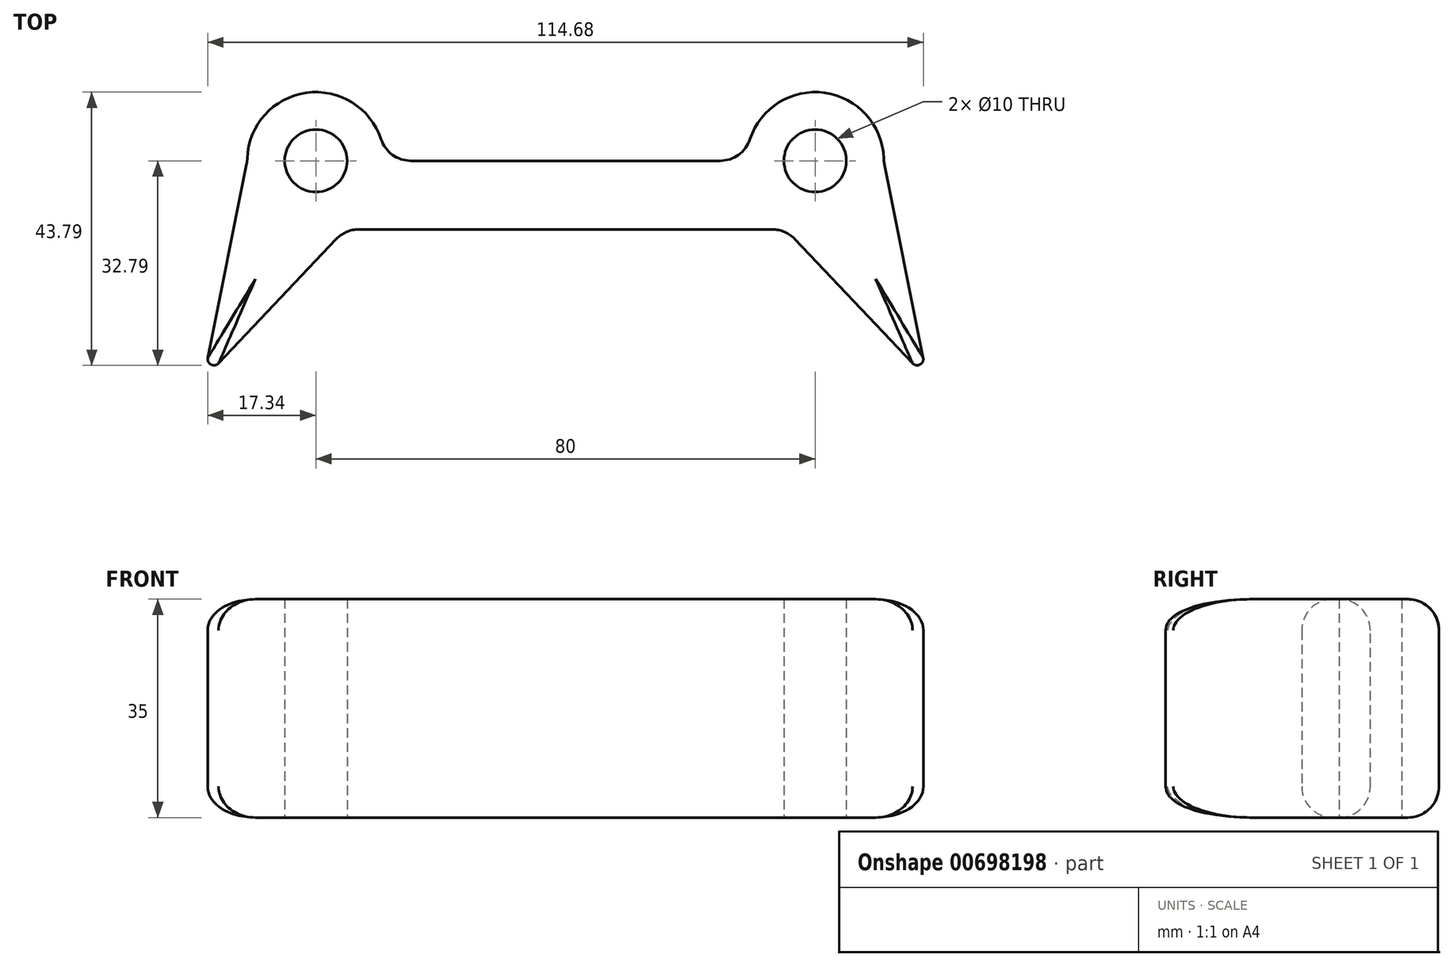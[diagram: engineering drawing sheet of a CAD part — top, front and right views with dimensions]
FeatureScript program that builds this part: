
annotation { "Feature Type Name" : "Feature", "Feature Type Description" : "" }
export const myFeature = defineFeature(function(context is Context, id is Id, definition is map)
    precondition{}
    {
        {
            var Q0;
            Q0=qCreatedBy(makeId("Top.planeOp"),FACE);
            var sketch = newSketch(context, id + "F0", { "sketchPlane" : qUnion([Q0])});
            skCircle(sketch, "E0", {"center": v(-40, 0) * mm, "radius": 5 * mm});
            skLineSegment(sketch, "E1", {"start": v(-35.27, -11) * mm, "end": v(0, -11) * mm});
            skLineSegment(sketch, "E2", {"start": v(-29, 0) * mm, "end": v(0, 0) * mm});
            skLineSegment(sketch, "E3", {"start": v(-51, 0) * mm, "end": v(-58, -35) * mm});
            skLineSegment(sketch, "E4", {"start": v(-58, -35) * mm, "end": v(-35.27, -11) * mm});
            skArc(sketch, "E5.trimOffspring", {"start": v(-29, 0) * mm, "mid": v(-40, 11) * mm, "end": v(-51, 0) * mm});
            skCircle(sketch, "E6.MirrorC", {"center": v(40, 0) * mm, "radius": 5 * mm});
            skLineSegment(sketch, "E7.MirrorCS", {"start": v(35.27, -11) * mm, "end": v(0, -11) * mm});
            skLineSegment(sketch, "E8.MirrorCS", {"start": v(29, 0) * mm, "end": v(0, 0) * mm});
            skLineSegment(sketch, "E9.MirrorCS", {"start": v(51, 0) * mm, "end": v(58, -35) * mm});
            skLineSegment(sketch, "E10.MirrorCS", {"start": v(58, -35) * mm, "end": v(35.27, -11) * mm});
            skArc(sketch, "E11.MirrorCS", {"start": v(29, 0) * mm, "mid": v(40, 11) * mm, "end": v(51, 0) * mm});
            skSolve(sketch);
        }
        {
            var Q0;
            Q0 = qSketchRegion(id + "F0", true);
            extrude(context, id + "F1", {"entities" : qUnion([Q0]), "depth" : 35 * mm, "offsetDistance" : 25 * mm});
        }
        {
            var Q0;
            Q0=makeQuery(id+"F1.opExtrude","SWEPT_EDGE",EDGE,{"disambiguationData":[OSD([sQuery(id+"F0.wireOp",EDGE,"E3"),sQuery(id+"F0.wireOp",EDGE,"E5.trimOffspring")])]});
            var Q1;
            Q1=makeQuery(id+"F1.opExtrude","SWEPT_EDGE",EDGE,{"disambiguationData":[OSD([sQuery(id+"F0.wireOp",EDGE,"E1"),sQuery(id+"F0.wireOp",EDGE,"E4")])]});
            var Q2;
            Q2=makeQuery(id+"F1.opExtrude","SWEPT_EDGE",EDGE,{"disambiguationData":[OSD([sQuery(id+"F0.wireOp",EDGE,"E7.MirrorCS"),sQuery(id+"F0.wireOp",EDGE,"E10.MirrorCS")])]});
            var Q3;
            Q3=makeQuery(id+"F1.opExtrude","SWEPT_EDGE",EDGE,{"disambiguationData":[OSD([sQuery(id+"F0.wireOp",EDGE,"E9.MirrorCS"),sQuery(id+"F0.wireOp",EDGE,"E11.MirrorCS")])]});
            var Q4;
            Q4=makeQuery(id+"F1.opExtrude","SWEPT_EDGE",EDGE,{"disambiguationData":[OSD([sQuery(id+"F0.wireOp",EDGE,"E2"),sQuery(id+"F0.wireOp",EDGE,"E5.trimOffspring")])]});
            var Q5;
            Q5=makeQuery(id+"F1.opExtrude","SWEPT_EDGE",EDGE,{"disambiguationData":[OSD([sQuery(id+"F0.wireOp",EDGE,"E8.MirrorCS"),sQuery(id+"F0.wireOp",EDGE,"E11.MirrorCS")])]});
            fillet(context, id + "F2", {"entities" : qUnion([Q0, Q1, Q2, Q3, Q4, Q5]), "radius" : 5 * mm, "tangentPropagation" : true, "allowEdgeOverflow" : false});
        }
        {
            var Q0;
            Q0=makeQuery(id+"F1.opExtrude","CAP_EDGE",EDGE,{"disambiguationData":[OSD([sQuery(id+"F0.wireOp",EDGE,"E9.MirrorCS")])],"isStart":false});
            var Q1;
            Q1=makeQuery(id+"F1.opExtrude","CAP_EDGE",EDGE,{"disambiguationData":[OSD([sQuery(id+"F0.wireOp",EDGE,"E9.MirrorCS")])],"isStart":true});
            var Q2;
            Q2=makeQuery(id+"F1.opExtrude","CAP_EDGE",EDGE,{"disambiguationData":[OSD([sQuery(id+"F0.wireOp",EDGE,"E10.MirrorCS")])],"isStart":true});
            var Q3;
            Q3=makeQuery(id+"F1.opExtrude","CAP_EDGE",EDGE,{"disambiguationData":[OSD([sQuery(id+"F0.wireOp",EDGE,"E1"),sQuery(id+"F0.wireOp",EDGE,"E7.MirrorCS")])],"isStart":false});
            fillet(context, id + "F3", {"entities" : qUnion([Q0, Q1, Q2, Q3]), "radius" : 5 * mm, "tangentPropagation" : true, "allowEdgeOverflow" : false});
        }
        {
            var Q0;
            Q0=makeQuery(id+"F1.opExtrude","SWEPT_EDGE",EDGE,{"disambiguationData":[OSD([sQuery(id+"F0.wireOp",EDGE,"E9.MirrorCS"),sQuery(id+"F0.wireOp",EDGE,"E10.MirrorCS")])]});
            var Q1;
            Q1=makeQuery(id+"F1.opExtrude","SWEPT_EDGE",EDGE,{"disambiguationData":[OSD([sQuery(id+"F0.wireOp",EDGE,"E3"),sQuery(id+"F0.wireOp",EDGE,"E4")])]});
            fillet(context, id + "F4", {"entities" : qUnion([Q0, Q1]), "radius" : 1 * mm, "tangentPropagation" : true, "allowEdgeOverflow" : false});
        }
    });
